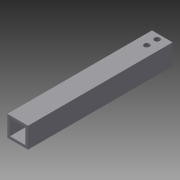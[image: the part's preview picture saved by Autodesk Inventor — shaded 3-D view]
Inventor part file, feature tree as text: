
AUTODESK INVENTOR PART (.ipt)
format: ipt  version: 2013 (Build 170138000, 138)  size: 96,768 bytes
history: native  units: in
note: dims shown in document units (in); Inventor stores cm internally (conversion verified against a paired STEP export)
features: extrude x2, sketch x2, reference x2
ambient origin geometry x8: Origin, YZ Plane, XZ Plane, XY Plane, X Axis, Y Axis, Z Axis, Center Point
bodies: Solid1 (feature_tree)
feature tree (6):
  extrude  "Extrusion1"  Depth=1.0in
  extrude  "Extrusion2"  Depth=7.0in TaperAngle=0.0deg
  sketch  "Sketch1"  dims[d0=1.0in d2=1.0in]
  sketch  "Sketch2"  dims[d3=0.125in d4=7.0in d5=0.0in d6=1.0in d7=0.0in]
  reference  "Reference1"
  reference  "Reference2"
